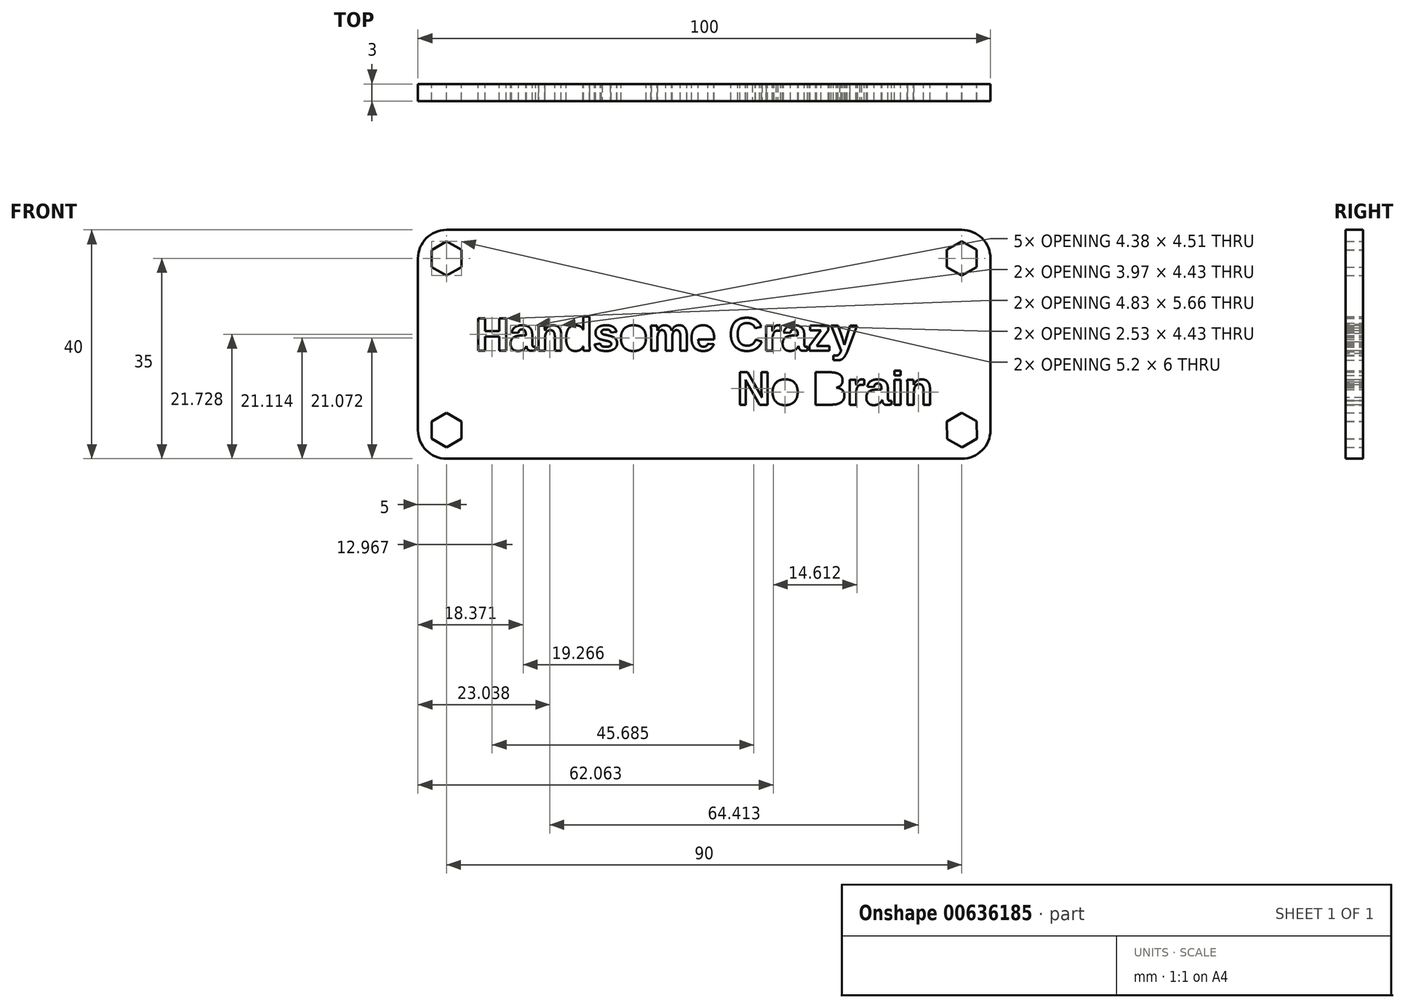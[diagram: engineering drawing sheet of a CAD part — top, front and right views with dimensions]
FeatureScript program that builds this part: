
annotation { "Feature Type Name" : "Feature", "Feature Type Description" : "" }
export const myFeature = defineFeature(function(context is Context, id is Id, definition is map)
    precondition{}
    {
        {
            var Q0;
            Q0=qCreatedBy(makeId("Front.planeOp"),FACE);
            var sketch = newSketch(context, id + "F0", { "sketchPlane" : qUnion([Q0])});
            skLineSegment(sketch, "E0.top", {"start": v(5, -40) * mm, "end": v(95, -40) * mm});
            skLineSegment(sketch, "E0.left", {"start": v(0, -5) * mm, "end": v(0, -35) * mm});
            skLineSegment(sketch, "E0.right", {"start": v(100, -5) * mm, "end": v(100, -35) * mm});
            skPoint(sketch, "E1.visualSharp", {"position": v(0, 0) * mm});
            skArc(sketch, "E1.filletArc", {"start": v(5, 0) * mm, "mid": v(1.46, -1.46) * mm, "end": v(0, -5) * mm});
            skPoint(sketch, "E2.visualSharp", {"position": v(100, 0) * mm});
            skArc(sketch, "E2.filletArc", {"start": v(100, -5) * mm, "mid": v(98.54, -1.46) * mm, "end": v(95, 0) * mm});
            skPoint(sketch, "E3.visualSharp", {"position": v(100, -40) * mm});
            skArc(sketch, "E3.filletArc", {"start": v(95, -40) * mm, "mid": v(98.54, -38.54) * mm, "end": v(100, -35) * mm});
            skPoint(sketch, "E4.visualSharp", {"position": v(0, -40) * mm});
            skArc(sketch, "E4.filletArc", {"start": v(0, -35) * mm, "mid": v(1.46, -38.54) * mm, "end": v(5, -40) * mm});
            skText(sketch, "E5", { "text": "Handsome Crazy \n                    No Brain", "fontName": "Arimo-Bold.ttf"});
            skLineSegment(sketch, "E6", {"start": v(10, -15.19) * mm, "end": v(10, -0.19) * mm, "construction": true});
            skLineSegment(sketch, "E7", {"start": v(10, -15.19) * mm, "end": v(0, -15.19) * mm, "construction": true});
            skCircle(sketch, "E8", {"center": v(5, -5) * mm, "radius": 1.5 * mm});
            skLineSegment(sketch, "E9", {"start": v(5, -5) * mm, "end": v(5, 0) * mm, "construction": true});
            skLineSegment(sketch, "E10", {"start": v(5, 0) * mm, "end": v(5, -5) * mm, "construction": true});
            skLineSegment(sketch, "E11", {"start": v(0, -5) * mm, "end": v(5, -5) * mm, "construction": true});
            skLineSegment(sketch, "E12", {"start": v(50, 0) * mm, "end": v(50, -40) * mm, "construction": true});
            skCircle(sketch, "E13.MirrorC", {"center": v(95, -5) * mm, "radius": 1.5 * mm});
            skLineSegment(sketch, "E14", {"start": v(0, -20) * mm, "end": v(100, -20) * mm, "construction": true});
            skCircle(sketch, "E15.MirrorC", {"center": v(5, -35) * mm, "radius": 1.5 * mm});
            skCircle(sketch, "E16.MirrorC", {"center": v(95, -35) * mm, "radius": 1.5 * mm});
            skLineSegment(sketch, "E17", {"start": v(5, 0) * mm, "end": v(95, 0) * mm});
            skCircle(sketch, "E18.cCircle", {"center": v(95, -5) * mm, "radius": 2.6 * mm, "construction": true});
            skLineSegment(sketch, "E18.0", {"start": v(97.6, -3.5) * mm, "end": v(97.6, -6.5) * mm});
            skLineSegment(sketch, "E18.1", {"start": v(97.6, -6.5) * mm, "end": v(95, -8) * mm});
            skLineSegment(sketch, "E18.2", {"start": v(95, -8) * mm, "end": v(92.4, -6.5) * mm});
            skLineSegment(sketch, "E18.3", {"start": v(92.4, -6.5) * mm, "end": v(92.4, -3.5) * mm});
            skLineSegment(sketch, "E18.4", {"start": v(92.4, -3.5) * mm, "end": v(95, -2) * mm});
            skLineSegment(sketch, "E18.5", {"start": v(95, -2) * mm, "end": v(97.6, -3.5) * mm});
            skPoint(sketch, "E18.0.midPoint", {"position": v(97.6, -5) * mm});
            skCircle(sketch, "E19.cCircle", {"center": v(95, -35) * mm, "radius": 2.6 * mm, "construction": true});
            skLineSegment(sketch, "E19.0", {"start": v(94.96, -32) * mm, "end": v(97.58, -33.47) * mm});
            skLineSegment(sketch, "E19.1", {"start": v(97.58, -33.47) * mm, "end": v(97.62, -36.46) * mm});
            skLineSegment(sketch, "E19.2", {"start": v(97.62, -36.46) * mm, "end": v(95.04, -38) * mm});
            skLineSegment(sketch, "E19.3", {"start": v(95.04, -38) * mm, "end": v(92.42, -36.53) * mm});
            skLineSegment(sketch, "E19.4", {"start": v(92.42, -36.53) * mm, "end": v(92.38, -33.54) * mm});
            skLineSegment(sketch, "E19.5", {"start": v(92.38, -33.54) * mm, "end": v(94.96, -32) * mm});
            skPoint(sketch, "E19.0.midPoint", {"position": v(96.27, -32.73) * mm});
            skCircle(sketch, "E20.cCircle", {"center": v(5, -5) * mm, "radius": 2.6 * mm, "construction": true});
            skLineSegment(sketch, "E20.0", {"start": v(5, -2) * mm, "end": v(7.6, -3.5) * mm});
            skLineSegment(sketch, "E20.1", {"start": v(7.6, -3.5) * mm, "end": v(7.6, -6.5) * mm});
            skLineSegment(sketch, "E20.2", {"start": v(7.6, -6.5) * mm, "end": v(5, -8) * mm});
            skLineSegment(sketch, "E20.3", {"start": v(5, -8) * mm, "end": v(2.4, -6.5) * mm});
            skLineSegment(sketch, "E20.4", {"start": v(2.4, -6.5) * mm, "end": v(2.4, -3.5) * mm});
            skLineSegment(sketch, "E20.5", {"start": v(2.4, -3.5) * mm, "end": v(5, -2) * mm});
            skPoint(sketch, "E20.0.midPoint", {"position": v(6.3, -2.75) * mm});
            skCircle(sketch, "E21.cCircle", {"center": v(5, -35) * mm, "radius": 2.6 * mm, "construction": true});
            skLineSegment(sketch, "E21.0", {"start": v(4.98, -32) * mm, "end": v(7.59, -33.48) * mm});
            skLineSegment(sketch, "E21.1", {"start": v(7.59, -33.48) * mm, "end": v(7.6, -36.48) * mm});
            skLineSegment(sketch, "E21.2", {"start": v(7.6, -36.48) * mm, "end": v(5.02, -38) * mm});
            skLineSegment(sketch, "E21.3", {"start": v(5.02, -38) * mm, "end": v(2.41, -36.52) * mm});
            skLineSegment(sketch, "E21.4", {"start": v(2.41, -36.52) * mm, "end": v(2.4, -33.52) * mm});
            skLineSegment(sketch, "E21.5", {"start": v(2.4, -33.52) * mm, "end": v(4.98, -32) * mm});
            skPoint(sketch, "E21.0.midPoint", {"position": v(6.29, -32.74) * mm});
            const initialGuessF0  = {"E5": [0.01, -0.0211, 1, 0, 0.00592]};
            skSetInitialGuess(sketch, initialGuessF0);
            skSolve(sketch);
        }
        {
            var Q0;
            Q0 = qSketchRegion(id + "F0", true);
            extrude(context, id + "F1", {"entities" : qUnion([Q0]), "depth" : 3 * mm, "offsetDistance" : 25 * mm});
        }
    });
